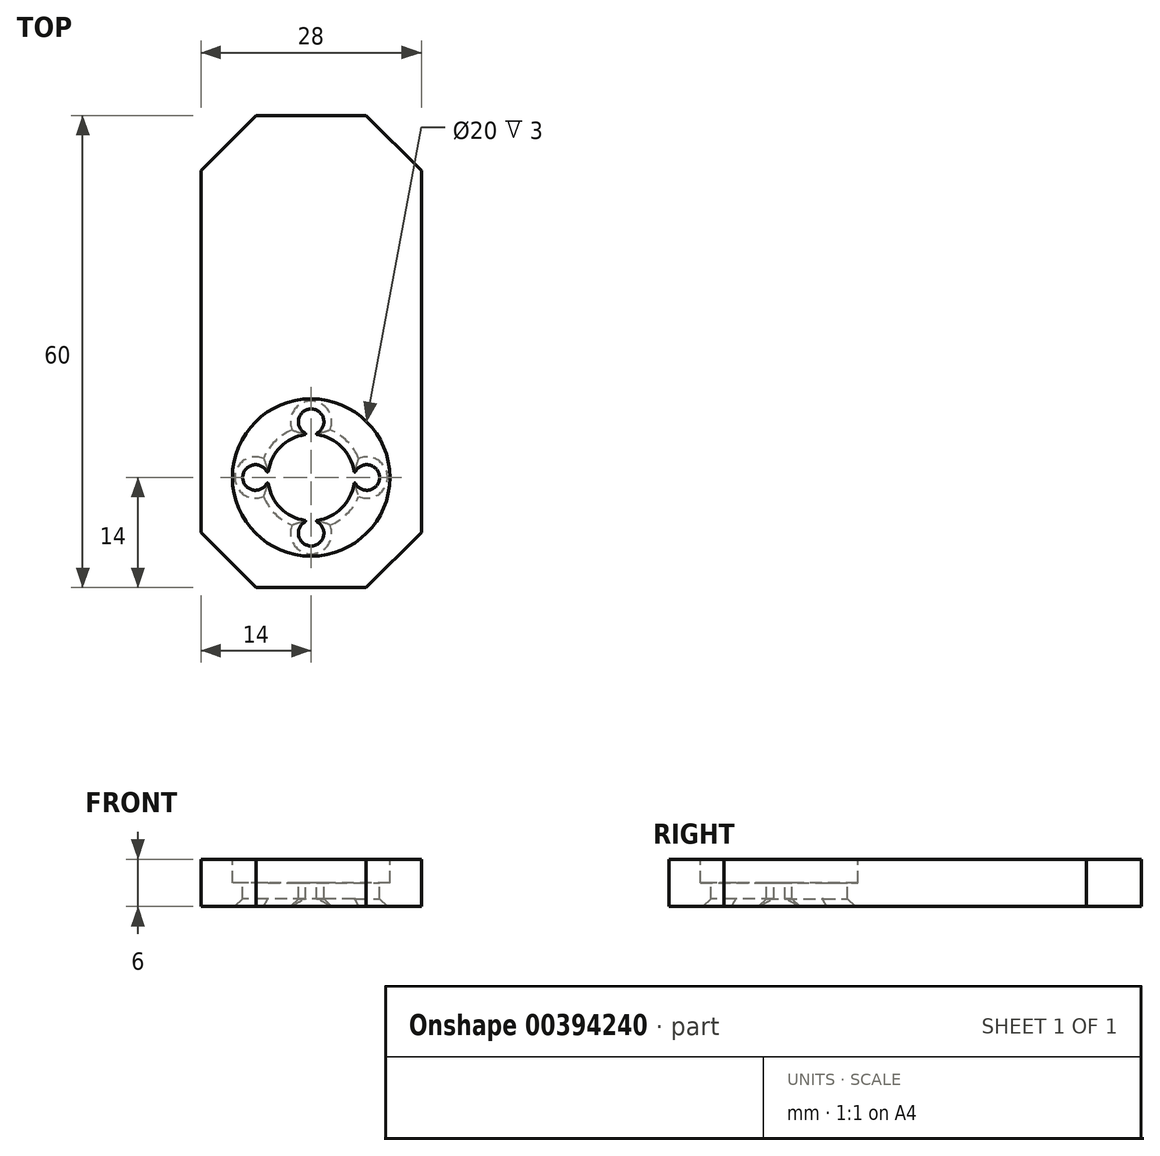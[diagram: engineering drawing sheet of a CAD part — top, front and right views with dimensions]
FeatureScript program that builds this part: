
annotation { "Feature Type Name" : "Feature", "Feature Type Description" : "" }
export const myFeature = defineFeature(function(context is Context, id is Id, definition is map)
    precondition{}
    {
        {
            var Q0;
            Q0=qCreatedBy(makeId("Top.planeOp"),FACE);
            var sketch = newSketch(context, id + "F0", { "sketchPlane" : qUnion([Q0])});
            skLineSegment(sketch, "E0.bottom", {"start": v(-14, 46) * mm, "end": v(14, 46) * mm});
            skLineSegment(sketch, "E0.top", {"start": v(-14, -14) * mm, "end": v(14, -14) * mm});
            skLineSegment(sketch, "E0.left", {"start": v(-14, 46) * mm, "end": v(-14, -14) * mm});
            skLineSegment(sketch, "E0.right", {"start": v(14, 46) * mm, "end": v(14, -14) * mm});
            skLineSegment(sketch, "E1", {"start": v(0, 50.42) * mm, "end": v(0, -18.38) * mm, "construction": true});
            skLineSegment(sketch, "E2", {"start": v(-18.38, 0) * mm, "end": v(19.17, 0) * mm, "construction": true});
            skSolve(sketch);
        }
        {
            var Q0;
            Q0 = qSketchRegion(id + "F0", true);
            extrude(context, id + "F1", {"entities" : qUnion([Q0]), "depth" : 6 * mm, "offsetDistance" : 25 * mm});
        }
        {
            var Q0;
            Q0=makeQuery(id+"F1.opExtrude","CAP_FACE",FACE,{"disambiguationData":[OSD([sQuery(id+"F0.wireOp",EDGE,"E0.bottom"),sQuery(id+"F0.wireOp",EDGE,"E0.top"),sQuery(id+"F0.wireOp",EDGE,"E0.left"),sQuery(id+"F0.wireOp",EDGE,"E0.right")])],"isStart":false});
            var sketch = newSketch(context, id + "F2", { "sketchPlane" : qUnion([Q0])});
            skCircle(sketch, "E3", {"center": v(0, 0) * mm, "radius": 10 * mm});
            skSolve(sketch);
        }
        {
            var Q0;
            Q0 = qSketchRegion(id + "F2", true);
            extrude(context, id + "F3", {"entities" : qUnion([Q0]), "operationType" : NewBodyOperationType.REMOVE, "oppositeDirection" : true, "depth" : 3 * mm, "offsetDistance" : 25 * mm});
        }
        {
            var Q0;
            Q0=makeQuery(id+"F3.boolean.opBoolean","COPY",FACE,{"derivedFrom":makeQuery(id+"F3.opExtrude","CAP_FACE",FACE,{"disambiguationData":[OSD([sQuery(id+"F2.wireOp",EDGE,"E3")])],"isStart":false})});
            var sketch = newSketch(context, id + "F4", { "sketchPlane" : qUnion([Q0])});
            skCircle(sketch, "E4", {"center": v(0, 0) * mm, "radius": 5.5 * mm});
            skCircle(sketch, "E5", {"center": v(0, 0) * mm, "radius": 7.07 * mm, "construction": true});
            skCircle(sketch, "E6", {"center": v(0, 7.07) * mm, "radius": 1.63 * mm});
            skCircle(sketch, "E7.1.0", {"center": v(7.07, 0) * mm, "radius": 1.63 * mm});
            skCircle(sketch, "E7.2.0", {"center": v(0, -7.07) * mm, "radius": 1.63 * mm});
            skLineSegment(sketch, "E7.anchor1", {"start": v(0, 0) * mm, "end": v(0, 7.07) * mm, "construction": true});
            skLineSegment(sketch, "E7.anchor2", {"start": v(0, 0) * mm, "end": v(-7.07, 0) * mm, "construction": true});
            skCircle(sketch, "E8.1.3.0", {"center": v(-7.07, 0) * mm, "radius": 1.63 * mm});
            skSolve(sketch);
        }
        {
            var Q0;
            Q0 = qSketchRegion(id + "F4", true);
            extrude(context, id + "F5", {"entities" : qUnion([Q0]), "operationType" : NewBodyOperationType.REMOVE, "endBound" : BoundingType.THROUGH_ALL, "oppositeDirection" : true, "depth" : 25 * mm, "offsetDistance" : 25 * mm});
        }
        {
            var Q0;
            Q0=makeQuery(id+"F5.boolean.opBoolean","INTERSECT",EDGE,{"derivedFrom":[makeQuery(id+"F1.opExtrude","CAP_FACE",FACE,{"disambiguationData":[OSD([sQuery(id+"F0.wireOp",EDGE,"E0.bottom"),sQuery(id+"F0.wireOp",EDGE,"E0.top"),sQuery(id+"F0.wireOp",EDGE,"E0.left"),sQuery(id+"F0.wireOp",EDGE,"E0.right")])],"isStart":true}),makeQuery(id+"F5.opExtrude","SWEPT_FACE",FACE,{"disambiguationData":[OSD([sQuery(id+"F4.wireOp",EDGE,"E4")])]})]});
            var Q1;
            Q1=makeQuery(id+"F5.boolean.opBoolean","INTERSECT",EDGE,{"derivedFrom":[makeQuery(id+"F1.opExtrude","CAP_FACE",FACE,{"disambiguationData":[OSD([sQuery(id+"F0.wireOp",EDGE,"E0.bottom"),sQuery(id+"F0.wireOp",EDGE,"E0.top"),sQuery(id+"F0.wireOp",EDGE,"E0.left"),sQuery(id+"F0.wireOp",EDGE,"E0.right")])],"isStart":true}),makeQuery(id+"F5.opExtrude","SWEPT_FACE",FACE,{"disambiguationData":[OSD([sQuery(id+"F4.wireOp",EDGE,"E7.2.0")])]})]});
            var Q2;
            Q2=makeQuery(id+"F5.boolean.opBoolean","INTERSECT",EDGE,{"derivedFrom":[makeQuery(id+"F1.opExtrude","CAP_FACE",FACE,{"disambiguationData":[OSD([sQuery(id+"F0.wireOp",EDGE,"E0.bottom"),sQuery(id+"F0.wireOp",EDGE,"E0.top"),sQuery(id+"F0.wireOp",EDGE,"E0.left"),sQuery(id+"F0.wireOp",EDGE,"E0.right")])],"isStart":true}),makeQuery(id+"F5.opExtrude","SWEPT_FACE",FACE,{"disambiguationData":[OSD([sQuery(id+"F4.wireOp",EDGE,"E7.1.0")])]})]});
            var Q3;
            Q3=makeQuery(id+"F5.boolean.opBoolean","INTERSECT",EDGE,{"derivedFrom":[makeQuery(id+"F1.opExtrude","CAP_FACE",FACE,{"disambiguationData":[OSD([sQuery(id+"F0.wireOp",EDGE,"E0.bottom"),sQuery(id+"F0.wireOp",EDGE,"E0.top"),sQuery(id+"F0.wireOp",EDGE,"E0.left"),sQuery(id+"F0.wireOp",EDGE,"E0.right")])],"isStart":true}),makeQuery(id+"F5.opExtrude","SWEPT_FACE",FACE,{"disambiguationData":[OSD([sQuery(id+"F4.wireOp",EDGE,"E8.1.3.0")])]})]});
            var Q4;
            Q4=makeQuery(id+"F5.boolean.opBoolean","INTERSECT",EDGE,{"derivedFrom":[makeQuery(id+"F1.opExtrude","CAP_FACE",FACE,{"disambiguationData":[OSD([sQuery(id+"F0.wireOp",EDGE,"E0.bottom"),sQuery(id+"F0.wireOp",EDGE,"E0.top"),sQuery(id+"F0.wireOp",EDGE,"E0.left"),sQuery(id+"F0.wireOp",EDGE,"E0.right")])],"isStart":true}),makeQuery(id+"F5.opExtrude","SWEPT_FACE",FACE,{"disambiguationData":[OSD([sQuery(id+"F4.wireOp",EDGE,"E6")])]})]});
            chamfer(context, id + "F6", {"entities" : qUnion([Q0, Q1, Q2, Q3, Q4]), "width" : 1 * mm, "tangentPropagation" : true});
        }
        {
            var Q0;
            Q0=makeQuery(id+"F1.opExtrude","SWEPT_EDGE",EDGE,{"disambiguationData":[OSD([sQuery(id+"F0.wireOp",EDGE,"E0.top"),sQuery(id+"F0.wireOp",EDGE,"E0.right")])]});
            var Q1;
            Q1=makeQuery(id+"F1.opExtrude","SWEPT_EDGE",EDGE,{"disambiguationData":[OSD([sQuery(id+"F0.wireOp",EDGE,"E0.top"),sQuery(id+"F0.wireOp",EDGE,"E0.left")])]});
            var Q2;
            Q2=makeQuery(id+"F1.opExtrude","SWEPT_EDGE",EDGE,{"disambiguationData":[OSD([sQuery(id+"F0.wireOp",EDGE,"E0.bottom"),sQuery(id+"F0.wireOp",EDGE,"E0.right")])]});
            var Q3;
            Q3=makeQuery(id+"F1.opExtrude","SWEPT_EDGE",EDGE,{"disambiguationData":[OSD([sQuery(id+"F0.wireOp",EDGE,"E0.bottom"),sQuery(id+"F0.wireOp",EDGE,"E0.left")])]});
            chamfer(context, id + "F7", {"entities" : qUnion([Q0, Q1, Q2, Q3]), "width" : 7 * mm, "tangentPropagation" : true});
        }
        {
            var Q0;
            {var subQ0=sQuery(id+"F4.wireOp",EDGE,"E6");var subQ1=sQuery(id+"F4.wireOp",EDGE,"E4");Q0=makeQuery(id+"F5.boolean.opBoolean","COPY",EDGE,{"derivedFrom":makeQuery(id+"F5.opExtrude","SWEPT_EDGE",EDGE,{"disambiguationData":[OSD([subQ1,subQ0]),TDD([makeQuery(id+"F4.imprint","INTERSECT",VERTEX,{"disambiguationData":[OD(1.0)],"derivedFrom":[subQ1,subQ0]})])]})});}
            var Q1;
            {var subQ0=sQuery(id+"F4.wireOp",EDGE,"E8.1.3.0");var subQ1=sQuery(id+"F4.wireOp",EDGE,"E4");Q1=makeQuery(id+"F5.boolean.opBoolean","COPY",EDGE,{"derivedFrom":makeQuery(id+"F5.opExtrude","SWEPT_EDGE",EDGE,{"disambiguationData":[OSD([subQ1,subQ0]),TDD([makeQuery(id+"F4.imprint","INTERSECT",VERTEX,{"disambiguationData":[OD(0.0)],"derivedFrom":[subQ1,subQ0]})])]})});}
            var Q2;
            {var subQ0=sQuery(id+"F4.wireOp",EDGE,"E8.1.3.0");var subQ1=sQuery(id+"F4.wireOp",EDGE,"E4");Q2=makeQuery(id+"F5.boolean.opBoolean","COPY",EDGE,{"derivedFrom":makeQuery(id+"F5.opExtrude","SWEPT_EDGE",EDGE,{"disambiguationData":[OSD([subQ1,subQ0]),TDD([makeQuery(id+"F4.imprint","INTERSECT",VERTEX,{"disambiguationData":[OD(1.0)],"derivedFrom":[subQ1,subQ0]})])]})});}
            var Q3;
            {var subQ0=sQuery(id+"F4.wireOp",EDGE,"E6");var subQ1=sQuery(id+"F4.wireOp",EDGE,"E4");Q3=makeQuery(id+"F5.boolean.opBoolean","COPY",EDGE,{"derivedFrom":makeQuery(id+"F5.opExtrude","SWEPT_EDGE",EDGE,{"disambiguationData":[OSD([subQ1,subQ0]),TDD([makeQuery(id+"F4.imprint","INTERSECT",VERTEX,{"disambiguationData":[OD(0.0)],"derivedFrom":[subQ1,subQ0]})])]})});}
            var Q4;
            {var subQ0=sQuery(id+"F4.wireOp",EDGE,"E7.1.0");var subQ1=sQuery(id+"F4.wireOp",EDGE,"E4");Q4=makeQuery(id+"F5.boolean.opBoolean","COPY",EDGE,{"derivedFrom":makeQuery(id+"F5.opExtrude","SWEPT_EDGE",EDGE,{"disambiguationData":[OSD([subQ1,subQ0]),TDD([makeQuery(id+"F4.imprint","INTERSECT",VERTEX,{"disambiguationData":[OD(0.0)],"derivedFrom":[subQ1,subQ0]})])]})});}
            var Q5;
            {var subQ0=sQuery(id+"F4.wireOp",EDGE,"E7.1.0");var subQ1=sQuery(id+"F4.wireOp",EDGE,"E4");Q5=makeQuery(id+"F5.boolean.opBoolean","COPY",EDGE,{"derivedFrom":makeQuery(id+"F5.opExtrude","SWEPT_EDGE",EDGE,{"disambiguationData":[OSD([subQ1,subQ0]),TDD([makeQuery(id+"F4.imprint","INTERSECT",VERTEX,{"disambiguationData":[OD(1.0)],"derivedFrom":[subQ1,subQ0]})])]})});}
            var Q6;
            {var subQ0=sQuery(id+"F4.wireOp",EDGE,"E7.2.0");var subQ1=sQuery(id+"F4.wireOp",EDGE,"E4");Q6=makeQuery(id+"F5.boolean.opBoolean","COPY",EDGE,{"derivedFrom":makeQuery(id+"F5.opExtrude","SWEPT_EDGE",EDGE,{"disambiguationData":[OSD([subQ1,subQ0]),TDD([makeQuery(id+"F4.imprint","INTERSECT",VERTEX,{"disambiguationData":[OD(0.0)],"derivedFrom":[subQ1,subQ0]})])]})});}
            var Q7;
            {var subQ0=sQuery(id+"F4.wireOp",EDGE,"E7.2.0");var subQ1=sQuery(id+"F4.wireOp",EDGE,"E4");Q7=makeQuery(id+"F5.boolean.opBoolean","COPY",EDGE,{"derivedFrom":makeQuery(id+"F5.opExtrude","SWEPT_EDGE",EDGE,{"disambiguationData":[OSD([subQ1,subQ0]),TDD([makeQuery(id+"F4.imprint","INTERSECT",VERTEX,{"disambiguationData":[OD(1.0)],"derivedFrom":[subQ1,subQ0]})])]})});}
            fillet(context, id + "F8", {"entities" : qUnion([Q0, Q1, Q2, Q3, Q4, Q5, Q6, Q7]), "tangentPropagation" : true, "radius" : 0.1 * mm, "defaultsChanged" : false, "vertexSettings" : [], "allowEdgeOverflow" : false});
        }
    });
